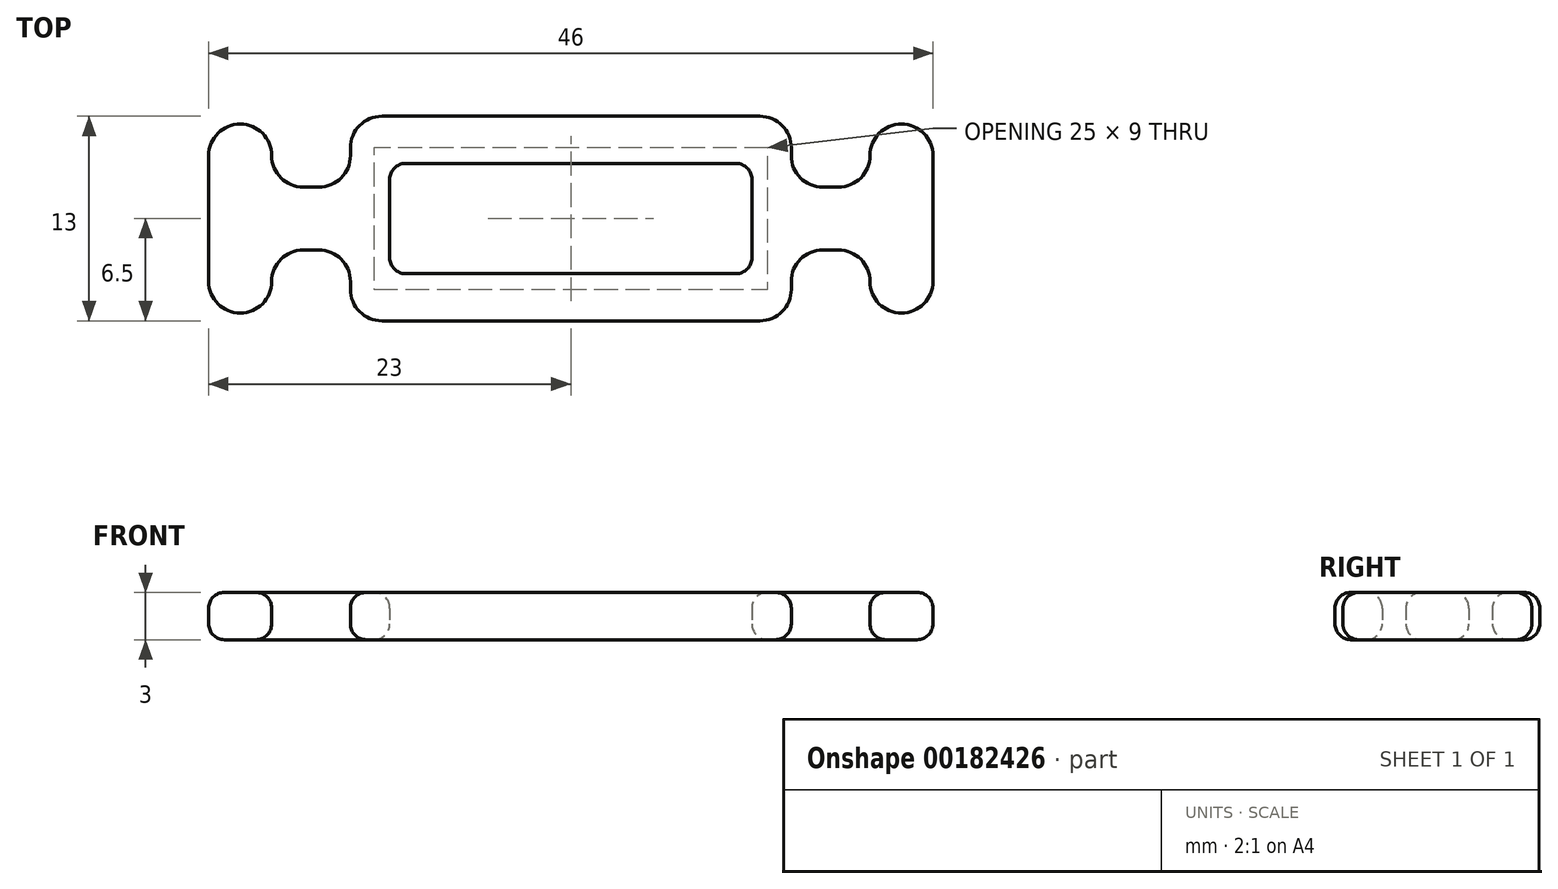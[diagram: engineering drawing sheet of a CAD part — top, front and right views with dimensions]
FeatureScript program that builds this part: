
annotation { "Feature Type Name" : "Feature", "Feature Type Description" : "" }
export const myFeature = defineFeature(function(context is Context, id is Id, definition is map)
    precondition{}
    {
        {
            var Q0;
            Q0=qCreatedBy(makeId("Top.planeOp"),FACE);
            var sketch = newSketch(context, id + "F0", { "sketchPlane" : qUnion([Q0])});
            skLineSegment(sketch, "E0.left", {"start": v(11.5, 3.5) * mm, "end": v(11.5, -3.5) * mm});
            skLineSegment(sketch, "E0.right", {"start": v(-11.5, 3.5) * mm, "end": v(-11.5, -3.5) * mm});
            skPoint(sketch, "E0.middle", {"position": v(0, 0) * mm});
            skLineSegment(sketch, "E1.0", {"start": v(-14, 6.5) * mm, "end": v(-14, 2) * mm});
            skLineSegment(sketch, "E1.1", {"start": v(14, 6.5) * mm, "end": v(-14, 6.5) * mm});
            skLineSegment(sketch, "E1.2", {"start": v(14, 6.5) * mm, "end": v(14, 2) * mm});
            skLineSegment(sketch, "E1.3", {"start": v(14, -6.5) * mm, "end": v(-14, -6.5) * mm});
            skLineSegment(sketch, "E2.trimOffspring", {"start": v(11.5, -3.5) * mm, "end": v(-11.5, -3.5) * mm});
            skLineSegment(sketch, "E3.trimOffspring", {"start": v(11.5, 3.5) * mm, "end": v(-11.5, 3.5) * mm});
            skLineSegment(sketch, "E4", {"start": v(14, 2) * mm, "end": v(19, 2) * mm});
            skLineSegment(sketch, "E5", {"start": v(19, 2) * mm, "end": v(19, 6) * mm});
            skLineSegment(sketch, "E6", {"start": v(19, 6) * mm, "end": v(23, 6) * mm});
            skLineSegment(sketch, "E7", {"start": v(23, 6) * mm, "end": v(23, 0) * mm});
            skPoint(sketch, "E7.endSnap0", {"position": v(14, 0) * mm});
            skLineSegment(sketch, "E8.MirrorCS", {"start": v(19, -2) * mm, "end": v(19, -6) * mm});
            skLineSegment(sketch, "E9.MirrorCS", {"start": v(14, -2) * mm, "end": v(19, -2) * mm});
            skLineSegment(sketch, "E10.MirrorCS", {"start": v(23, -6) * mm, "end": v(23, 0) * mm});
            skLineSegment(sketch, "E11.MirrorCS", {"start": v(19, -6) * mm, "end": v(23, -6) * mm});
            skLineSegment(sketch, "E12.trimOffspring", {"start": v(14, -2) * mm, "end": v(14, -6.5) * mm});
            skLineSegment(sketch, "E13.MirrorCS", {"start": v(-23, 6) * mm, "end": v(-23, 0) * mm});
            skLineSegment(sketch, "E14.MirrorCS", {"start": v(-19, 6) * mm, "end": v(-23, 6) * mm});
            skLineSegment(sketch, "E15.MirrorCS", {"start": v(-14, -2) * mm, "end": v(-19, -2) * mm});
            skLineSegment(sketch, "E16.MirrorCS", {"start": v(-19, 2) * mm, "end": v(-19, 6) * mm});
            skLineSegment(sketch, "E17.MirrorCS", {"start": v(-19, -6) * mm, "end": v(-23, -6) * mm});
            skLineSegment(sketch, "E18.MirrorCS", {"start": v(-19, -2) * mm, "end": v(-19, -6) * mm});
            skLineSegment(sketch, "E19.MirrorCS", {"start": v(-23, -6) * mm, "end": v(-23, 0) * mm});
            skLineSegment(sketch, "E20.MirrorCS", {"start": v(-14, 2) * mm, "end": v(-19, 2) * mm});
            skLineSegment(sketch, "E21.trimOffspring", {"start": v(-14, -2) * mm, "end": v(-14, -6.5) * mm});
            skSolve(sketch);
        }
        {
            var Q0;
            Q0=makeQuery(id+"F0.imprint","IMPRINT",FACE,{"disambiguationData":[TD([[makeQuery(id+"F0.imprint","IMPRINT",EDGE,{"derivedFrom":sQuery(id+"F0.wireOp",EDGE,"E0.left")}),1.0]])]});
            extrude(context, id + "F1", {"entities" : qUnion([Q0]), "depth" : 3 * mm});
        }
        {
            var Q0;
            Q0=makeQuery(id+"F1.opExtrude","SWEPT_EDGE",EDGE,{"disambiguationData":[OSD([sQuery(id+"F0.wireOp",EDGE,"E1.2"),sQuery(id+"F0.wireOp",EDGE,"E1.3")])]});
            var Q1;
            Q1=makeQuery(id+"F1.opExtrude","SWEPT_EDGE",EDGE,{"disambiguationData":[OSD([sQuery(id+"F0.wireOp",EDGE,"E1.1"),sQuery(id+"F0.wireOp",EDGE,"E1.2")])]});
            var Q2;
            Q2=makeQuery(id+"F1.opExtrude","SWEPT_EDGE",EDGE,{"disambiguationData":[OSD([sQuery(id+"F0.wireOp",EDGE,"E1.0"),sQuery(id+"F0.wireOp",EDGE,"E1.3")])]});
            var Q3;
            Q3=makeQuery(id+"F1.opExtrude","SWEPT_EDGE",EDGE,{"disambiguationData":[OSD([sQuery(id+"F0.wireOp",EDGE,"E1.0"),sQuery(id+"F0.wireOp",EDGE,"E1.1")])]});
            var Q4;
            Q4=makeQuery(id+"F1.opExtrude","SWEPT_EDGE",EDGE,{"disambiguationData":[OSD([sQuery(id+"F0.wireOp",EDGE,"E9.MirrorCS"),sQuery(id+"F0.wireOp",EDGE,"E12.trimOffspring")])]});
            var Q5;
            Q5=makeQuery(id+"F1.opExtrude","SWEPT_EDGE",EDGE,{"disambiguationData":[OSD([sQuery(id+"F0.wireOp",EDGE,"E15.MirrorCS"),sQuery(id+"F0.wireOp",EDGE,"E21.trimOffspring")])]});
            var Q6;
            Q6=makeQuery(id+"F1.opExtrude","SWEPT_EDGE",EDGE,{"disambiguationData":[OSD([sQuery(id+"F0.wireOp",EDGE,"E8.MirrorCS"),sQuery(id+"F0.wireOp",EDGE,"E9.MirrorCS")])]});
            var Q7;
            Q7=makeQuery(id+"F1.opExtrude","SWEPT_EDGE",EDGE,{"disambiguationData":[OSD([sQuery(id+"F0.wireOp",EDGE,"E4"),sQuery(id+"F0.wireOp",EDGE,"E5")])]});
            var Q8;
            Q8=makeQuery(id+"F1.opExtrude","SWEPT_EDGE",EDGE,{"disambiguationData":[OSD([sQuery(id+"F0.wireOp",EDGE,"E16.MirrorCS"),sQuery(id+"F0.wireOp",EDGE,"E20.MirrorCS")])]});
            var Q9;
            Q9=makeQuery(id+"F1.opExtrude","SWEPT_EDGE",EDGE,{"disambiguationData":[OSD([sQuery(id+"F0.wireOp",EDGE,"E15.MirrorCS"),sQuery(id+"F0.wireOp",EDGE,"E18.MirrorCS")])]});
            var Q10;
            Q10=makeQuery(id+"F1.opExtrude","SWEPT_EDGE",EDGE,{"disambiguationData":[OSD([sQuery(id+"F0.wireOp",EDGE,"E17.MirrorCS"),sQuery(id+"F0.wireOp",EDGE,"E18.MirrorCS")])]});
            var Q11;
            Q11=makeQuery(id+"F1.opExtrude","SWEPT_EDGE",EDGE,{"disambiguationData":[OSD([sQuery(id+"F0.wireOp",EDGE,"E17.MirrorCS"),sQuery(id+"F0.wireOp",EDGE,"E19.MirrorCS")])]});
            var Q12;
            Q12=makeQuery(id+"F1.opExtrude","SWEPT_EDGE",EDGE,{"disambiguationData":[OSD([sQuery(id+"F0.wireOp",EDGE,"E13.MirrorCS"),sQuery(id+"F0.wireOp",EDGE,"E14.MirrorCS")])]});
            var Q13;
            Q13=makeQuery(id+"F1.opExtrude","SWEPT_EDGE",EDGE,{"disambiguationData":[OSD([sQuery(id+"F0.wireOp",EDGE,"E8.MirrorCS"),sQuery(id+"F0.wireOp",EDGE,"E11.MirrorCS")])]});
            var Q14;
            Q14=makeQuery(id+"F1.opExtrude","SWEPT_EDGE",EDGE,{"disambiguationData":[OSD([sQuery(id+"F0.wireOp",EDGE,"E10.MirrorCS"),sQuery(id+"F0.wireOp",EDGE,"E11.MirrorCS")])]});
            var Q15;
            Q15=makeQuery(id+"F1.opExtrude","SWEPT_EDGE",EDGE,{"disambiguationData":[OSD([sQuery(id+"F0.wireOp",EDGE,"E14.MirrorCS"),sQuery(id+"F0.wireOp",EDGE,"E16.MirrorCS")])]});
            var Q16;
            Q16=makeQuery(id+"F1.opExtrude","SWEPT_EDGE",EDGE,{"disambiguationData":[OSD([sQuery(id+"F0.wireOp",EDGE,"E5"),sQuery(id+"F0.wireOp",EDGE,"E6")])]});
            var Q17;
            Q17=makeQuery(id+"F1.opExtrude","SWEPT_EDGE",EDGE,{"disambiguationData":[OSD([sQuery(id+"F0.wireOp",EDGE,"E6"),sQuery(id+"F0.wireOp",EDGE,"E7")])]});
            fillet(context, id + "F2", {"entities" : qUnion([Q0, Q1, Q2, Q3, Q4, Q5, Q6, Q7, Q8, Q9, Q10, Q11, Q12, Q13, Q14, Q15, Q16, Q17]), "radius" : 2 * mm, "tangentPropagation" : true, "allowEdgeOverflow" : false});
        }
        {
            var Q0;
            Q0=makeQuery(id+"F1.opExtrude","SWEPT_EDGE",EDGE,{"disambiguationData":[OSD([sQuery(id+"F0.wireOp",EDGE,"E0.bottom"),sQuery(id+"F0.wireOp",EDGE,"zzJNbanq-JphB-Kgf2-X89a-ZxSrZC5uSn7O.left")])]});
            var Q1;
            Q1=makeQuery(id+"F1.opExtrude","SWEPT_EDGE",EDGE,{"disambiguationData":[OSD([sQuery(id+"F0.wireOp",EDGE,"E0.right"),sQuery(id+"F0.wireOp",EDGE,"E3.trimOffspring")])]});
            var Q2;
            Q2=makeQuery(id+"F1.opExtrude","SWEPT_EDGE",EDGE,{"disambiguationData":[OSD([sQuery(id+"F0.wireOp",EDGE,"E0.top"),sQuery(id+"F0.wireOp",EDGE,"zzJNbanq-JphB-Kgf2-X89a-ZxSrZC5uSn7O.left")])]});
            var Q3;
            Q3=makeQuery(id+"F1.opExtrude","SWEPT_EDGE",EDGE,{"disambiguationData":[OSD([sQuery(id+"F0.wireOp",EDGE,"E0.right"),sQuery(id+"F0.wireOp",EDGE,"E2.trimOffspring")])]});
            var Q4;
            Q4=makeQuery(id+"F1.opExtrude","SWEPT_FACE",FACE,{"disambiguationData":[OSD([sQuery(id+"F0.wireOp",EDGE,"E0.top")])]});
            var Q5;
            Q5=makeQuery(id+"F1.opExtrude","SWEPT_EDGE",EDGE,{"disambiguationData":[OSD([sQuery(id+"F0.wireOp",EDGE,"E0.bottom"),sQuery(id+"F0.wireOp",EDGE,"E0.left")])]});
            var Q6;
            Q6=makeQuery(id+"F1.opExtrude","CAP_FACE",FACE,{"disambiguationData":[OSD([sQuery(id+"F0.wireOp",EDGE,"E0.bottom"),sQuery(id+"F0.wireOp",EDGE,"E0.top"),sQuery(id+"F0.wireOp",EDGE,"E0.left"),sQuery(id+"F0.wireOp",EDGE,"E0.right"),sQuery(id+"F0.wireOp",EDGE,"E1.0"),sQuery(id+"F0.wireOp",EDGE,"E1.1"),sQuery(id+"F0.wireOp",EDGE,"E1.2"),sQuery(id+"F0.wireOp",EDGE,"E1.3"),sQuery(id+"F0.wireOp",EDGE,"zzJNbanq-JphB-Kgf2-X89a-ZxSrZC5uSn7O.left"),sQuery(id+"F0.wireOp",EDGE,"zzJNbanq-JphB-Kgf2-X89a-ZxSrZC5uSn7O.right"),sQuery(id+"F0.wireOp",EDGE,"E2.trimOffspring"),sQuery(id+"F0.wireOp",EDGE,"E3.trimOffspring")])],"isStart":true});
            var Q7;
            Q7=makeQuery(id+"F1.opExtrude","CAP_FACE",FACE,{"disambiguationData":[OSD([sQuery(id+"F0.wireOp",EDGE,"E0.bottom"),sQuery(id+"F0.wireOp",EDGE,"E0.top"),sQuery(id+"F0.wireOp",EDGE,"E0.left"),sQuery(id+"F0.wireOp",EDGE,"E0.right"),sQuery(id+"F0.wireOp",EDGE,"E1.0"),sQuery(id+"F0.wireOp",EDGE,"E1.1"),sQuery(id+"F0.wireOp",EDGE,"E1.2"),sQuery(id+"F0.wireOp",EDGE,"E1.3"),sQuery(id+"F0.wireOp",EDGE,"zzJNbanq-JphB-Kgf2-X89a-ZxSrZC5uSn7O.left"),sQuery(id+"F0.wireOp",EDGE,"zzJNbanq-JphB-Kgf2-X89a-ZxSrZC5uSn7O.right"),sQuery(id+"F0.wireOp",EDGE,"E2.trimOffspring"),sQuery(id+"F0.wireOp",EDGE,"E3.trimOffspring")])],"isStart":false});
            var Q8;
            Q8=makeQuery(id+"F1.opExtrude","SWEPT_EDGE",EDGE,{"disambiguationData":[OSD([sQuery(id+"F0.wireOp",EDGE,"zzJNbanq-JphB-Kgf2-X89a-ZxSrZC5uSn7O.right"),sQuery(id+"F0.wireOp",EDGE,"E2.trimOffspring")])]});
            var Q9;
            Q9=makeQuery(id+"F1.opExtrude","SWEPT_EDGE",EDGE,{"disambiguationData":[OSD([sQuery(id+"F0.wireOp",EDGE,"zzJNbanq-JphB-Kgf2-X89a-ZxSrZC5uSn7O.right"),sQuery(id+"F0.wireOp",EDGE,"E3.trimOffspring")])]});
            fillet(context, id + "F3", {"entities" : qUnion([Q0, Q1, Q2, Q3, Q4, Q5, Q6, Q7, Q8, Q9]), "radius" : 1 * mm, "tangentPropagation" : true, "allowEdgeOverflow" : false});
        }
    });
